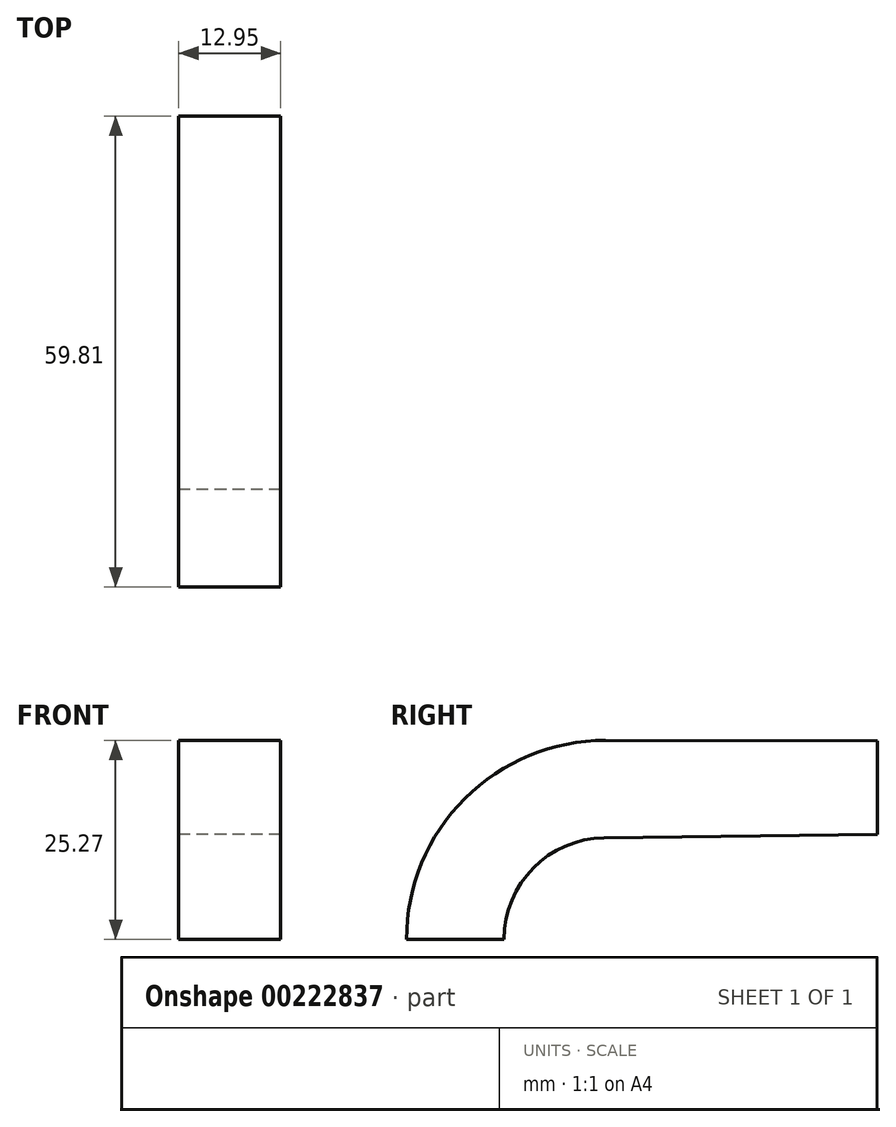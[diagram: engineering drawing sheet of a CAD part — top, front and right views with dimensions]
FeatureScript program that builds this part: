
annotation { "Feature Type Name" : "Feature", "Feature Type Description" : "" }
export const myFeature = defineFeature(function(context is Context, id is Id, definition is map)
    precondition{}
    {
        {
            var Q0;
            Q0=qCreatedBy(makeId("Right.planeOp"),FACE);
            var sketch = newSketch(context, id + "F0", { "sketchPlane" : qUnion([Q0])});
            skArc(sketch, "E0", {"start": v(0, 12.9) * mm, "mid": v(-9, 9.06) * mm, "end": v(-12.72, 0) * mm});
            skArc(sketch, "E1", {"start": v(0.17, 25.27) * mm, "mid": v(-17.7, 17.89) * mm, "end": v(-25.1, 0) * mm});
            skLineSegment(sketch, "E2", {"start": v(0.17, 25.27) * mm, "end": v(34.72, 25.2) * mm});
            skLineSegment(sketch, "E3", {"start": v(0, 12.9) * mm, "end": v(34.72, 13.36) * mm});
            skLineSegment(sketch, "E4", {"start": v(34.72, 25.2) * mm, "end": v(34.72, 13.36) * mm});
            skLineSegment(sketch, "E5", {"start": v(-12.72, 0) * mm, "end": v(-25.1, 0) * mm});
            skSolve(sketch);
        }
        {
            var Q0;
            Q0 = qSketchRegion(id + "F0", true);
            extrude(context, id + "F1", {"entities" : qUnion([Q0]), "depth" : 12.95 * mm});
        }
    });
